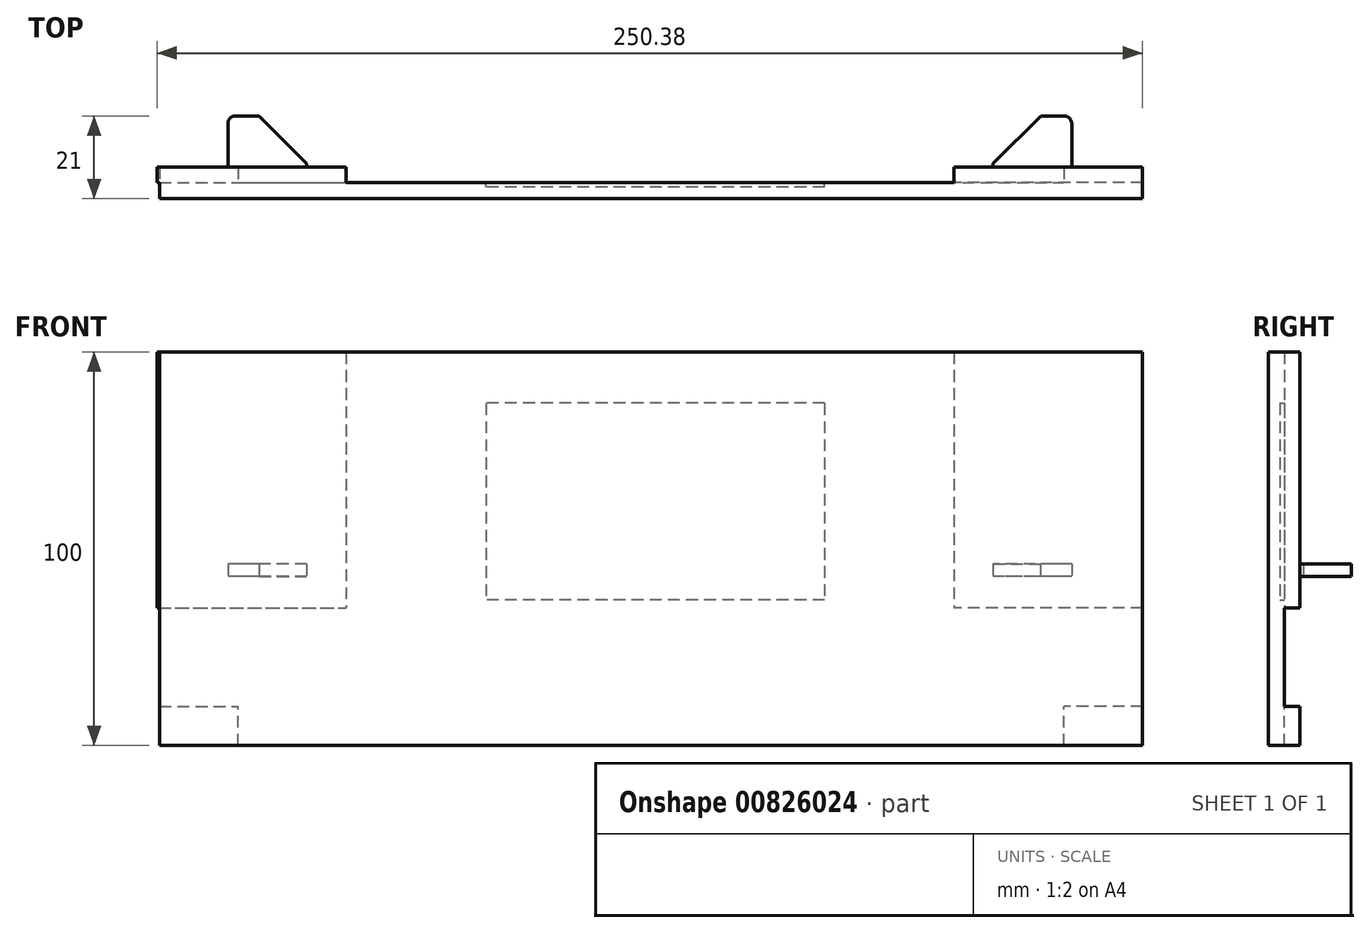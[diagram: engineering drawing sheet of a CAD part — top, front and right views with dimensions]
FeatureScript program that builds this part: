
annotation { "Feature Type Name" : "Feature", "Feature Type Description" : "" }
export const myFeature = defineFeature(function(context is Context, id is Id, definition is map)
    precondition{}
    {
        {
            var Q0;
            Q0=qCreatedBy(makeId("Front.planeOp"),FACE);
            var sketch = newSketch(context, id + "F0", { "sketchPlane" : qUnion([Q0])});
            skLineSegment(sketch, "E0.bottom", {"start": v(-124.61, 29.03) * mm, "end": v(125.19, 29.03) * mm});
            skLineSegment(sketch, "E0.top", {"start": v(-124.61, -70.97) * mm, "end": v(125.19, -70.97) * mm});
            skLineSegment(sketch, "E0.left", {"start": v(-124.61, 29.03) * mm, "end": v(-124.61, -70.97) * mm});
            skLineSegment(sketch, "E0.right", {"start": v(125.19, 29.03) * mm, "end": v(125.19, -70.97) * mm});
            skSolve(sketch);
        }
        {
            var Q0;
            Q0 = qSketchRegion(id + "F0", true);
            extrude(context, id + "F1", {"entities" : qUnion([Q0]), "depth" : 4 * mm, "offsetDistance" : 25 * mm});
        }
        {
            var Q0;
            Q0=makeQuery(id+"F1.opExtrude","CAP_FACE",FACE,{"disambiguationData":[OSD([sQuery(id+"F0.wireOp",EDGE,"E0.bottom"),sQuery(id+"F0.wireOp",EDGE,"E0.top"),sQuery(id+"F0.wireOp",EDGE,"E0.left"),sQuery(id+"F0.wireOp",EDGE,"E0.right")])],"isStart":true});
            var sketch = newSketch(context, id + "F2", { "sketchPlane" : qUnion([Q0])});
            skLineSegment(sketch, "E1.bottom", {"start": v(-44.39, 16.03) * mm, "end": v(41.61, 16.03) * mm});
            skLineSegment(sketch, "E1.top", {"start": v(-44.39, -33.97) * mm, "end": v(41.61, -33.97) * mm});
            skLineSegment(sketch, "E1.left", {"start": v(-44.39, 16.03) * mm, "end": v(-44.39, -33.97) * mm});
            skLineSegment(sketch, "E1.right", {"start": v(41.61, 16.03) * mm, "end": v(41.61, -33.97) * mm});
            skLineSegment(sketch, "E2.top", {"start": v(-63.39, -54.57) * mm, "end": v(60.31, -54.57) * mm});
            skLineSegment(sketch, "E2.left", {"start": v(-63.39, 20.93) * mm, "end": v(-63.39, -54.57) * mm});
            skLineSegment(sketch, "E2.right", {"start": v(60.31, 20.93) * mm, "end": v(60.31, -54.57) * mm});
            skLineSegment(sketch, "E3.bottom", {"start": v(-77.19, 29.03) * mm, "end": v(76.61, 29.03) * mm});
            skLineSegment(sketch, "E3.top", {"start": v(-77.19, -70.97) * mm, "end": v(76.61, -70.97) * mm});
            skLineSegment(sketch, "E3.left", {"start": v(-77.19, 29.03) * mm, "end": v(-77.19, -70.97) * mm});
            skLineSegment(sketch, "E3.right", {"start": v(76.61, 29.03) * mm, "end": v(76.61, -70.97) * mm});
            skLineSegment(sketch, "E4.left", {"start": v(-44.39, 6.03) * mm, "end": v(-44.39, -23.97) * mm});
            skLineSegment(sketch, "E5", {"start": v(-44.39, 6.03) * mm, "end": v(-44.39, 16.03) * mm});
            skLineSegment(sketch, "E6", {"start": v(41.61, 6.03) * mm, "end": v(41.61, 16.03) * mm});
            skLineSegment(sketch, "E7.trimOffspring", {"start": v(14.71, 20.93) * mm, "end": v(60.31, 20.93) * mm});
            skLineSegment(sketch, "E8", {"start": v(-63.39, 20.93) * mm, "end": v(60.31, 20.93) * mm});
            skSolve(sketch);
        }
        {
            var Q0;
            Q0=makeQuery(id+"F1.opExtrude","CAP_FACE",FACE,{"disambiguationData":[OSD([sQuery(id+"F0.wireOp",EDGE,"E0.bottom"),sQuery(id+"F0.wireOp",EDGE,"E0.top"),sQuery(id+"F0.wireOp",EDGE,"E0.left"),sQuery(id+"F0.wireOp",EDGE,"E0.right")])],"isStart":true});
            var sketch = newSketch(context, id + "F3", { "sketchPlane" : qUnion([Q0])});
            skSolve(sketch);
        }
        {
            var Q0;
            Q0=makeQuery(id+"F3.imprint","IMPRINT",FACE,{"disambiguationData":[TD([[makeQuery(id+"F3.imprint","IMPRINT",EDGE,{"derivedFrom":makeQuery(id+"F1.opExtrude","CAP_EDGE",EDGE,{"disambiguationData":[OSD([sQuery(id+"F0.wireOp",EDGE,"E0.bottom")])],"isStart":true})}),1.0]])]});
            var sketch = newSketch(context, id + "F4", { "sketchPlane" : qUnion([Q0])});
            skLineSegment(sketch, "E9", {"start": v(0, 0) * mm, "end": v(0, 16.85) * mm, "construction": true});
            skLineSegment(sketch, "E10", {"start": v(124.61, -20.97) * mm, "end": v(105.35, -20.97) * mm, "construction": true});
            skLineSegment(sketch, "E11.MirrorCS", {"start": v(124.61, -70.97) * mm, "end": v(124.61, -60.97) * mm});
            skLineSegment(sketch, "E12.MirrorCS", {"start": v(124.61, -70.97) * mm, "end": v(104.61, -70.97) * mm});
            skLineSegment(sketch, "E13.MirrorCS", {"start": v(104.61, -70.97) * mm, "end": v(104.61, -60.97) * mm});
            skLineSegment(sketch, "E14.MirrorCS", {"start": v(124.61, -60.97) * mm, "end": v(104.61, -60.97) * mm});
            skLineSegment(sketch, "E15.MirrorCS", {"start": v(-125.19, -70.97) * mm, "end": v(-125.19, -60.97) * mm});
            skLineSegment(sketch, "E16.MirrorCS", {"start": v(-125.19, -70.97) * mm, "end": v(-105.19, -70.97) * mm});
            skLineSegment(sketch, "E17.MirrorCS", {"start": v(-125.19, -60.97) * mm, "end": v(-105.19, -60.97) * mm});
            skLineSegment(sketch, "E18.MirrorCS", {"start": v(-105.19, -70.97) * mm, "end": v(-105.19, -60.97) * mm});
            skLineSegment(sketch, "E19.bottom", {"start": v(-125.19, 29.03) * mm, "end": v(-77.19, 29.03) * mm});
            skLineSegment(sketch, "E19.top", {"start": v(-125.19, -35.97) * mm, "end": v(-77.19, -35.97) * mm});
            skLineSegment(sketch, "E19.left", {"start": v(-125.19, 29.03) * mm, "end": v(-125.19, -35.97) * mm});
            skLineSegment(sketch, "E19.right", {"start": v(-77.19, 29.03) * mm, "end": v(-77.19, -35.97) * mm});
            skLineSegment(sketch, "E20.MirrorCS", {"start": v(125.19, -35.97) * mm, "end": v(77.19, -35.97) * mm});
            skLineSegment(sketch, "E21.MirrorCS", {"start": v(125.19, 29.03) * mm, "end": v(125.19, -35.97) * mm});
            skLineSegment(sketch, "E22.MirrorCS", {"start": v(77.19, 29.03) * mm, "end": v(77.19, -35.97) * mm});
            skLineSegment(sketch, "E23.MirrorCS", {"start": v(125.19, 29.03) * mm, "end": v(77.19, 29.03) * mm});
            skPoint(sketch, "E24.right.end.orphan", {"position": v(83.14, -60.97) * mm});
            skPoint(sketch, "E25.right.end.orphan", {"position": v(-85.19, -60.97) * mm});
            skSolve(sketch);
        }
        {
            var Q0;
            Q0=makeQuery(id+"F4.imprint","IMPRINT",FACE,{"disambiguationData":[TD([[makeQuery(id+"F4.imprint","IMPRINT",EDGE,{"derivedFrom":sQuery(id+"F4.wireOp",EDGE,"E15.MirrorCS")}),1.0]])]});
            var Q1;
            {var subQ0=sQuery(id+"F4.wireOp",EDGE,"293615f5-52cd-460a-92f3-f4d4d741ce071.MirrorCS");Q1=makeQuery(id+"F4.imprint","IMPRINT",FACE,{"disambiguationData":[TD([[makeQuery(id+"F4.imprint","IMPRINT",EDGE,{"derivedFrom":subQ0}),-1.0]])]});}
            var Q2;
            {var subQ0=sQuery(id+"F4.wireOp",EDGE,"E11.MirrorCS");Q2=makeQuery(id+"F4.imprint","IMPRINT",FACE,{"disambiguationData":[TD([[makeQuery(id+"F4.imprint","IMPRINT",EDGE,{"derivedFrom":subQ0}),1.0]])]});}
            var Q3;
            {var subQ0=sQuery(id+"F4.wireOp",EDGE,"293615f5-52cd-460a-92f3-f4d4d741ce072.MirrorCS");Q3=makeQuery(id+"F4.imprint","IMPRINT",FACE,{"disambiguationData":[TD([[makeQuery(id+"F4.imprint","IMPRINT",EDGE,{"derivedFrom":subQ0}),1.0]])]});}
            var Q4;
            {var subQ3=sQuery(id+"F4.wireOp",EDGE,"E13.MirrorCS");Q4=makeQuery(id+"F4.imprint","IMPRINT",FACE,{"disambiguationData":[TD([[makeQuery(id+"F4.imprint","IMPRINT",EDGE,{"derivedFrom":subQ3}),-1.0]])]});}
            var Q5;
            Q5=makeQuery(id+"F4.imprint","IMPRINT",FACE,{"disambiguationData":[TD([[makeQuery(id+"F4.imprint","IMPRINT",EDGE,{"derivedFrom":sQuery(id+"F4.wireOp",EDGE,"kk62LGye-nZwA-mlLW-wwsb-B3RobKQy4UYQ.bottom")}),1.0]])]});
            extrude(context, id + "F5", {"entities" : qUnion([Q0, Q1, Q2, Q3, Q4, Q5]), "operationType" : NewBodyOperationType.ADD, "depth" : 4 * mm, "offsetDistance" : 25 * mm});
        }
        {
            var Q0;
            Q0=makeQuery(id+"F3.imprint","IMPRINT",FACE,{"disambiguationData":[TD([[makeQuery(id+"F3.imprint","IMPRINT",EDGE,{"derivedFrom":makeQuery(id+"F1.opExtrude","CAP_EDGE",EDGE,{"disambiguationData":[OSD([sQuery(id+"F0.wireOp",EDGE,"E0.bottom")])],"isStart":true})}),1.0]])]});
            var sketch = newSketch(context, id + "F6", { "sketchPlane" : qUnion([Q0])});
            skLineSegment(sketch, "E26.bottom", {"start": v(-125.19, 29.03) * mm, "end": v(-77.19, 29.03) * mm});
            skLineSegment(sketch, "E26.top", {"start": v(-125.19, -35.97) * mm, "end": v(-77.19, -35.97) * mm});
            skLineSegment(sketch, "E26.left", {"start": v(-125.19, 29.03) * mm, "end": v(-125.19, -35.97) * mm});
            skLineSegment(sketch, "E26.right", {"start": v(-77.19, 29.03) * mm, "end": v(-77.19, -35.97) * mm});
            skLineSegment(sketch, "E27", {"start": v(0, 0) * mm, "end": v(0, 15.4) * mm, "construction": true});
            skLineSegment(sketch, "E28.MirrorCS", {"start": v(125.19, -35.97) * mm, "end": v(77.19, -35.97) * mm});
            skLineSegment(sketch, "E29.MirrorCS", {"start": v(125.19, 29.03) * mm, "end": v(125.19, -35.97) * mm});
            skLineSegment(sketch, "E30.MirrorCS", {"start": v(77.19, 29.03) * mm, "end": v(77.19, -35.97) * mm});
            skLineSegment(sketch, "E31.MirrorCS", {"start": v(125.19, 29.03) * mm, "end": v(77.19, 29.03) * mm});
            skSolve(sketch);
        }
        {
            var Q0;
            Q0 = qSketchRegion(id + "F6", true);
            extrude(context, id + "F7", {"entities" : qUnion([Q0]), "operationType" : NewBodyOperationType.ADD, "depth" : 4 * mm, "offsetDistance" : 25 * mm});
        }
        {
            var Q0;
            {var subQ0=sQuery(id+"F0.wireOp",EDGE,"E0.top");Q0=makeQuery(id+"F3.imprint","IMPRINT",FACE,{"disambiguationData":[TD([[makeQuery(id+"F3.imprint","IMPRINT",EDGE,{"derivedFrom":makeQuery(id+"F1.opExtrude","CAP_EDGE",EDGE,{"disambiguationData":[OSD([subQ0])],"isStart":true})}),-1.0]])]});}
            var sketch = newSketch(context, id + "F8", { "sketchPlane" : qUnion([Q0])});
            skLineSegment(sketch, "E32.bottom", {"start": v(124.61, -70.97) * mm, "end": v(104.61, -70.97) * mm});
            skLineSegment(sketch, "E32.top", {"start": v(124.61, -60.97) * mm, "end": v(104.61, -60.97) * mm});
            skLineSegment(sketch, "E32.left", {"start": v(124.61, -70.97) * mm, "end": v(124.61, -60.97) * mm});
            skLineSegment(sketch, "E32.right", {"start": v(104.61, -70.97) * mm, "end": v(104.61, -60.97) * mm});
            skSolve(sketch);
        }
        {
            var Q0;
            Q0 = qSketchRegion(id + "F8", true);
            extrude(context, id + "F9", {"entities" : qUnion([Q0]), "operationType" : NewBodyOperationType.ADD, "depth" : 4 * mm, "offsetDistance" : 25 * mm});
        }
        {
            var Q0;
            Q0=makeQuery(id+"F2.imprint","IMPRINT",FACE,{"disambiguationData":[TD([[makeQuery(id+"F2.imprint","IMPRINT",EDGE,{"derivedFrom":sQuery(id+"F2.wireOp",EDGE,"E1.bottom")}),-1.0]])]});
            extrude(context, id + "F10", {"entities" : qUnion([Q0]), "operationType" : NewBodyOperationType.REMOVE, "oppositeDirection" : true, "depth" : 1.1 * mm, "offsetDistance" : 25 * mm});
        }
        {
            var Q0;
            Q0=makeQuery(id+"F7.opExtrude","CAP_FACE",FACE,{"disambiguationData":[OSD([sQuery(id+"F6.wireOp",EDGE,"E26.bottom"),sQuery(id+"F6.wireOp",EDGE,"E26.top"),sQuery(id+"F6.wireOp",EDGE,"E26.left"),sQuery(id+"F6.wireOp",EDGE,"E26.right")])],"isStart":false});
            var sketch = newSketch(context, id + "F11", { "sketchPlane" : qUnion([Q0])});
            skLineSegment(sketch, "E33.bottom", {"start": v(-107.19, -24.77) * mm, "end": v(-87.19, -24.77) * mm});
            skLineSegment(sketch, "E33.top", {"start": v(-107.19, -27.97) * mm, "end": v(-87.19, -27.97) * mm});
            skLineSegment(sketch, "E33.left", {"start": v(-107.19, -24.77) * mm, "end": v(-107.19, -27.97) * mm});
            skLineSegment(sketch, "E33.right", {"start": v(-87.19, -24.77) * mm, "end": v(-87.19, -27.97) * mm});
            skLineSegment(sketch, "E34.bottom", {"start": v(87.19, -24.77) * mm, "end": v(107.19, -24.77) * mm});
            skLineSegment(sketch, "E34.top", {"start": v(87.19, -27.97) * mm, "end": v(107.19, -27.97) * mm});
            skLineSegment(sketch, "E34.left", {"start": v(87.19, -24.77) * mm, "end": v(87.19, -27.97) * mm});
            skLineSegment(sketch, "E34.right", {"start": v(107.19, -24.77) * mm, "end": v(107.19, -27.97) * mm});
            skSolve(sketch);
        }
        {
            var Q0;
            Q0 = qSketchRegion(id + "F11", true);
            extrude(context, id + "F12", {"entities" : qUnion([Q0]), "operationType" : NewBodyOperationType.ADD, "depth" : 13 * mm, "offsetDistance" : 25 * mm});
        }
        {
            var Q0;
            Q0=makeQuery(id+"F12.opExtrude","CAP_EDGE",EDGE,{"disambiguationData":[OSD([sQuery(id+"F11.wireOp",EDGE,"E33.right")])],"isStart":false});
            var Q1;
            Q1=makeQuery(id+"F12.opExtrude","CAP_EDGE",EDGE,{"disambiguationData":[OSD([sQuery(id+"F11.wireOp",EDGE,"E34.left")])],"isStart":false});
            chamfer(context, id + "F13", {"entities" : qUnion([Q0, Q1]), "width" : 12.1 * mm, "tangentPropagation" : true});
        }
        {
            var Q0;
            Q0=makeQuery(id+"F12.opExtrude","CAP_EDGE",EDGE,{"disambiguationData":[OSD([sQuery(id+"F11.wireOp",EDGE,"E33.left")])],"isStart":false});
            var Q1;
            Q1=makeQuery(id+"F12.opExtrude","CAP_EDGE",EDGE,{"disambiguationData":[OSD([sQuery(id+"F11.wireOp",EDGE,"E34.right")])],"isStart":false});
            fillet(context, id + "F14", {"entities" : qUnion([Q0, Q1]), "radius" : 2 * mm, "tangentPropagation" : true, "allowEdgeOverflow" : false});
        }
    });
